# Revit family: Electrical_Distribution_ABB_Elbow-1200A-Bus-N3R-Outdoor_12-Inch
name_source: partatom
category: Electrical Equipment
units: mm (PartAtom-declared; Revit-internal decimal feet)

## family parameters
Cut with Voids When Loaded = No
Host = Face
OmniClass Number = 23.35.31.27
OmniClass Title = Power Distribution Units
Panel Configuration = Two Columns, Circuits Across
Part Type = Panelboard
Room Calculation Point = No
Round Connector Dimension = Use Diameter
Shared = No

## types (1)
- RELBOW312N3R
    Apparent Load = 0 VA
    Date Updated = 2023/09/07
    Default Elevation = 4' - 0"
    Description = Elbow - 12X12" 1200A Bus N3R Outdoor
    Enclosure = N3R Outdoor
    Horizontal Bus Amperage = 1200 A
    Manufacturer = ABB
    Model = RELBOW312N3R
    Number of Poles = 3
    Phase = 1-Phase or 3-Phase
    Power Factor = 0
    Primary material = ABB - Steel - White
    Product data url = https://www.bimobject.com
    URL = https://new.abb.com
    Version = 1
    Voltage = 120/240V or 208Y/120V
    Voltage (V) = 120 V
    z12 = Yes
    z16 = No
    zXYBase = 1' - 0 1/2"
    zXYTop = 1' - 0 1/2"

## geometry (parser evidence)
native form markers: Sweep x14
no freeform markers — native parametric forms only
